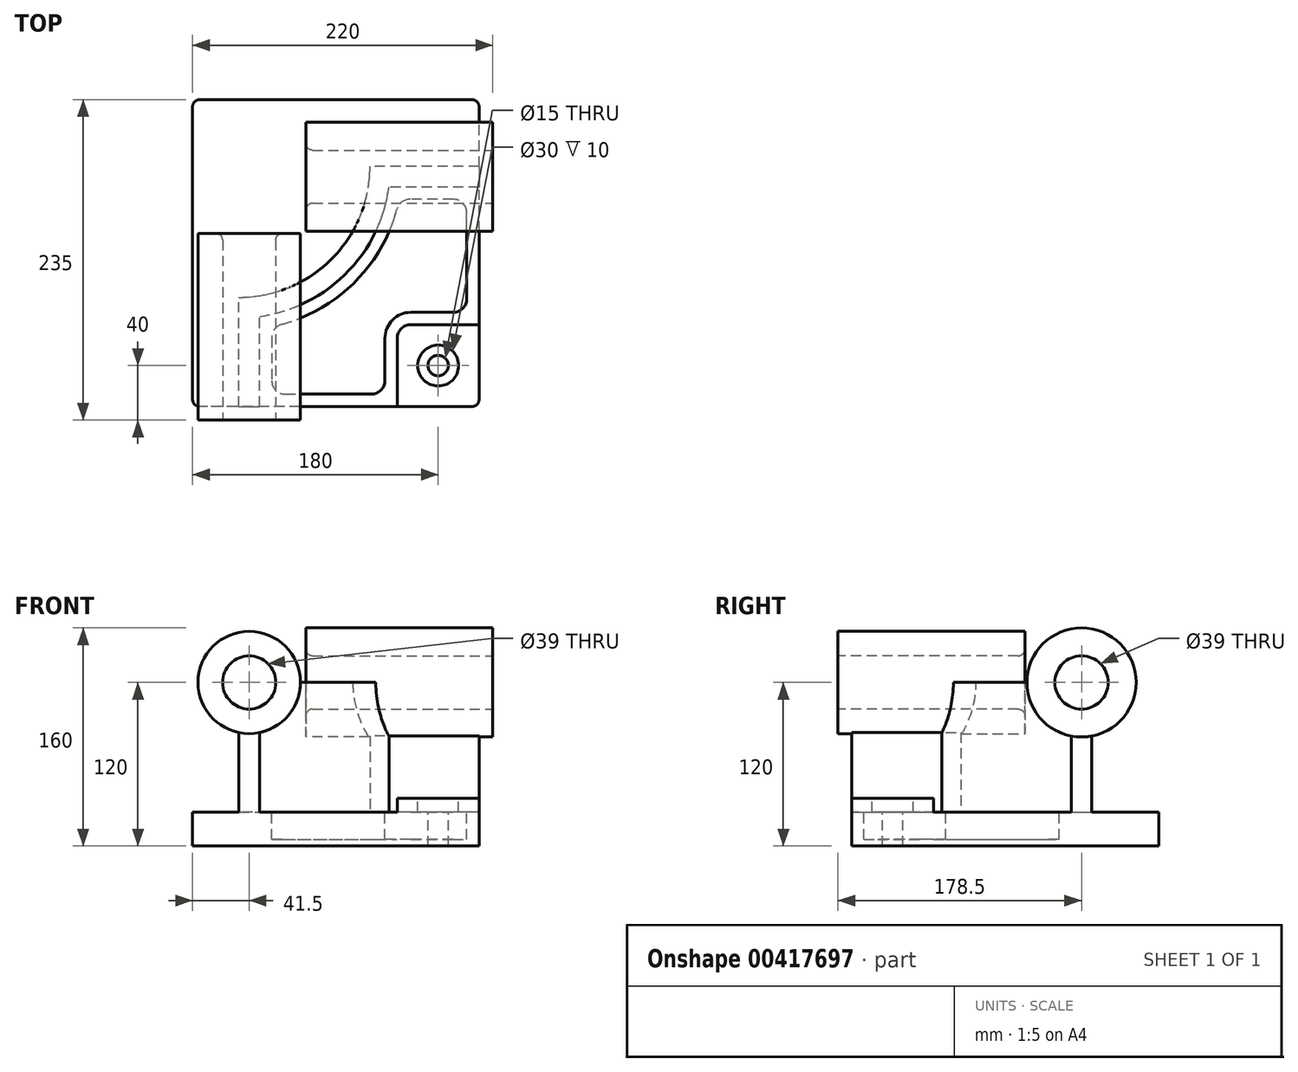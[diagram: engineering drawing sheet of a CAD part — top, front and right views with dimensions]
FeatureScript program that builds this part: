
annotation { "Feature Type Name" : "Feature", "Feature Type Description" : "" }
export const myFeature = defineFeature(function(context is Context, id is Id, definition is map)
    precondition{}
    {
        {
            var Q0;
            Q0=qCreatedBy(makeId("Top.planeOp"),FACE);
            var sketch = newSketch(context, id + "F0", { "sketchPlane" : qUnion([Q0])});
            skLineSegment(sketch, "E0.bottom", {"start": v(105, -112.5) * mm, "end": v(-105, -112.5) * mm});
            skLineSegment(sketch, "E0.top", {"start": v(105, 112.5) * mm, "end": v(-105, 112.5) * mm});
            skLineSegment(sketch, "E0.left", {"start": v(105, -112.5) * mm, "end": v(105, 112.5) * mm});
            skLineSegment(sketch, "E0.right", {"start": v(-105, -112.5) * mm, "end": v(-105, 112.5) * mm});
            skPoint(sketch, "E0.middle", {"position": v(0, 0) * mm});
            skSolve(sketch);
        }
        {
            var Q0;
            Q0=makeQuery(id+"F0.imprint","IMPRINT",FACE,{"disambiguationData":[TD([[makeQuery(id+"F0.imprint","IMPRINT",EDGE,{"derivedFrom":sQuery(id+"F0.wireOp",EDGE,"E0.bottom")}),-1.0]])]});
            extrude(context, id + "F1", {"entities" : qUnion([Q0]), "depth" : 25 * mm});
        }
        {
            var Q0;
            Q0=makeQuery(id+"F1.opExtrude","CAP_FACE",FACE,{"disambiguationData":[OSD([sQuery(id+"F0.wireOp",EDGE,"E0.bottom"),sQuery(id+"F0.wireOp",EDGE,"E0.top"),sQuery(id+"F0.wireOp",EDGE,"E0.left"),sQuery(id+"F0.wireOp",EDGE,"E0.right")])],"isStart":false});
            var sketch = newSketch(context, id + "F2", { "sketchPlane" : qUnion([Q0])});
            skLineSegment(sketch, "E1", {"start": v(-71, -112.5) * mm, "end": v(-71, -32.5) * mm});
            skLineSegment(sketch, "E2", {"start": v(105, 63.5) * mm, "end": v(25, 63.5) * mm});
            skArc(sketch, "E3", {"start": v(-71, -32.5) * mm, "mid": v(-3.12, -4.38) * mm, "end": v(25, 63.5) * mm});
            skLineSegment(sketch, "E4", {"start": v(-71, 63.5) * mm, "end": v(25, 63.5) * mm, "construction": true});
            skLineSegment(sketch, "E5", {"start": v(-71, 63.5) * mm, "end": v(-71, -32.5) * mm, "construction": true});
            skLineSegment(sketch, "E6.0", {"start": v(105, 48.5) * mm, "end": v(38.98, 48.5) * mm});
            skArc(sketch, "E6.1", {"start": v(-56, -46.48) * mm, "mid": v(7.49, -14.99) * mm, "end": v(38.98, 48.5) * mm});
            skLineSegment(sketch, "E6.2", {"start": v(-56, -112.5) * mm, "end": v(-56, -46.48) * mm});
            skLineSegment(sketch, "E7.0", {"start": v(105, -112.5) * mm, "end": v(-105, -112.5) * mm});
            skLineSegment(sketch, "E8.0", {"start": v(105, -112.5) * mm, "end": v(105, 112.5) * mm});
            skSolve(sketch);
        }
        {
            var Q0;
            {var subQ2=sQuery(id+"F2.wireOp",EDGE,"E1");Q0=makeQuery(id+"F2.imprint","IMPRINT",FACE,{"disambiguationData":[TD([[makeQuery(id+"F2.imprint","IMPRINT",EDGE,{"derivedFrom":subQ2}),-1.0]])]});}
            extrude(context, id + "F3", {"entities" : qUnion([Q0]), "operationType" : NewBodyOperationType.ADD, "depth" : 95 * mm});
        }
        {
            var Q0;
            Q0=makeQuery(id+"F3.boolean.opBoolean","MERGE",FACE,{"derivedFrom":[makeQuery(id+"F1.opExtrude","SWEPT_FACE",FACE,{"disambiguationData":[OSD([sQuery(id+"F0.wireOp",EDGE,"E0.bottom")])]}),makeQuery(id+"F3.opExtrude","SWEPT_FACE",FACE,{"disambiguationData":[OSD([sQuery(id+"F2.wireOp",EDGE,"E7.0")])]})]});
            var sketch = newSketch(context, id + "F4", { "sketchPlane" : qUnion([Q0])});
            skCircle(sketch, "E9", {"center": v(-63.5, 120) * mm, "radius": 37.5 * mm});
            skSolve(sketch);
        }
        {
            var Q0;
            Q0 = qSketchRegion(id + "F4", true);
            extrude(context, id + "F5", {"entities" : qUnion([Q0]), "operationType" : NewBodyOperationType.ADD, "depth" : 10 * mm, "hasSecondDirection" : true, "secondDirectionOppositeDirection" : true, "secondDirectionDepth" : 127 * mm});
        }
        {
            var Q0;
            Q0=makeQuery(id+"F3.boolean.opBoolean","MERGE",FACE,{"derivedFrom":[makeQuery(id+"F1.opExtrude","SWEPT_FACE",FACE,{"disambiguationData":[OSD([sQuery(id+"F0.wireOp",EDGE,"E0.left")])]}),makeQuery(id+"F3.opExtrude","SWEPT_FACE",FACE,{"disambiguationData":[OSD([sQuery(id+"F2.wireOp",EDGE,"E8.0")])]})]});
            var sketch = newSketch(context, id + "F6", { "sketchPlane" : qUnion([Q0])});
            skCircle(sketch, "E10", {"center": v(56, 120) * mm, "radius": 40 * mm});
            skSolve(sketch);
        }
        {
            var Q0;
            {var subQ1=sQuery(id+"F2.wireOp",EDGE,"E8.0");var subQ6=makeQuery(id+"F3.opExtrude","CAP_EDGE",EDGE,{"disambiguationData":[OSD([subQ1])],"isStart":false});Q0=makeQuery(id+"F6.imprint","IMPRINT",FACE,{"disambiguationData":[TD([[makeQuery(id+"F6.imprint","IMPRINT",EDGE,{"derivedFrom":subQ6}),-1.0]])]});}
            var Q1;
            {var subQ1=sQuery(id+"F2.wireOp",EDGE,"E8.0");var subQ6=makeQuery(id+"F3.opExtrude","CAP_EDGE",EDGE,{"disambiguationData":[OSD([subQ1])],"isStart":false});Q1=makeQuery(id+"F6.imprint","IMPRINT",FACE,{"disambiguationData":[TD([[makeQuery(id+"F6.imprint","IMPRINT",EDGE,{"derivedFrom":subQ6}),1.0]])]});}
            extrude(context, id + "F7", {"entities" : qUnion([Q0, Q1]), "operationType" : NewBodyOperationType.ADD, "depth" : 10 * mm, "hasSecondDirection" : true, "secondDirectionOppositeDirection" : true, "secondDirectionDepth" : 127 * mm});
        }
        {
            var Q0;
            {var subQ0=sQuery(id+"F0.wireOp",EDGE,"E0.left");var subQ1=sQuery(id+"F0.wireOp",EDGE,"E0.bottom");Q0=makeQuery(id+"F3.boolean.opBoolean","SPLIT",FACE,{"disambiguationData":[TD([makeQuery(id+"F3.opExtrude","SWEPT_FACE",FACE,{"disambiguationData":[OSD([sQuery(id+"F2.wireOp",EDGE,"E6.0")])]})])],"derivedFrom":makeQuery(id+"F1.opExtrude","CAP_FACE",FACE,{"disambiguationData":[OSD([subQ1,sQuery(id+"F0.wireOp",EDGE,"E0.top"),subQ0,sQuery(id+"F0.wireOp",EDGE,"E0.right")])],"isStart":false})});}
            var sketch = newSketch(context, id + "F8", { "sketchPlane" : qUnion([Q0])});
            skLineSegment(sketch, "E11.bottom", {"start": v(105, -112.5) * mm, "end": v(45, -112.5) * mm});
            skLineSegment(sketch, "E11.top", {"start": v(105, -52.5) * mm, "end": v(45, -52.5) * mm});
            skLineSegment(sketch, "E11.left", {"start": v(105, -112.5) * mm, "end": v(105, -52.5) * mm});
            skLineSegment(sketch, "E11.right", {"start": v(45, -112.5) * mm, "end": v(45, -52.5) * mm});
            skSolve(sketch);
        }
        {
            var Q0;
            Q0=makeQuery(id+"F8.imprint","IMPRINT",FACE,{"disambiguationData":[TD([[makeQuery(id+"F8.imprint","IMPRINT",EDGE,{"derivedFrom":sQuery(id+"F8.wireOp",EDGE,"E11.bottom")}),-1.0]])]});
            extrude(context, id + "F9", {"entities" : qUnion([Q0]), "operationType" : NewBodyOperationType.ADD, "depth" : 10 * mm});
        }
        {
            var Q0;
            Q0=makeQuery(id+"F9.opExtrude","SWEPT_EDGE",EDGE,{"disambiguationData":[OSD([sQuery(id+"F8.wireOp",EDGE,"E11.top"),sQuery(id+"F8.wireOp",EDGE,"E11.right")])]});
            fillet(context, id + "F10", {"entities" : qUnion([Q0]), "radius" : 10 * mm, "tangentPropagation" : true, "allowEdgeOverflow" : false});
        }
        {
            var Q0;
            {var subQ0=sQuery(id+"F0.wireOp",EDGE,"E0.left");var subQ1=sQuery(id+"F0.wireOp",EDGE,"E0.bottom");Q0=makeQuery(id+"F3.boolean.opBoolean","SPLIT",FACE,{"disambiguationData":[TD([makeQuery(id+"F3.opExtrude","SWEPT_FACE",FACE,{"disambiguationData":[OSD([sQuery(id+"F2.wireOp",EDGE,"E6.0")])]})])],"derivedFrom":makeQuery(id+"F1.opExtrude","CAP_FACE",FACE,{"disambiguationData":[OSD([subQ1,sQuery(id+"F0.wireOp",EDGE,"E0.top"),subQ0,sQuery(id+"F0.wireOp",EDGE,"E0.right")])],"isStart":false})});}
            var sketch = newSketch(context, id + "F11", { "sketchPlane" : qUnion([Q0])});
            skLineSegment(sketch, "E12.0", {"start": v(-47, -54.08) * mm, "end": v(-47, -103.5) * mm});
            skArc(sketch, "E12.1", {"start": v(46.58, 39.5) * mm, "mid": v(13.85, -21.35) * mm, "end": v(-47, -54.08) * mm});
            skLineSegment(sketch, "E12.2", {"start": v(-47, -103.5) * mm, "end": v(36, -103.5) * mm});
            skLineSegment(sketch, "E12.3", {"start": v(96, 39.5) * mm, "end": v(46.58, 39.5) * mm});
            skLineSegment(sketch, "E12.4", {"start": v(36, -103.5) * mm, "end": v(36, -62.5) * mm});
            skArc(sketch, "E12.5", {"start": v(36, -62.5) * mm, "mid": v(41.56, -49.06) * mm, "end": v(55, -43.5) * mm});
            skLineSegment(sketch, "E12.6", {"start": v(55, -43.5) * mm, "end": v(96, -43.5) * mm});
            skLineSegment(sketch, "E12.7", {"start": v(96, -43.5) * mm, "end": v(96, 39.5) * mm});
            skSolve(sketch);
        }
        {
            var Q0;
            Q0=makeQuery(id+"F11.imprint","IMPRINT",FACE,{"disambiguationData":[TD([[makeQuery(id+"F11.imprint","IMPRINT",EDGE,{"derivedFrom":sQuery(id+"F11.wireOp",EDGE,"E12.0")}),1.0]])]});
            extrude(context, id + "F12", {"entities" : qUnion([Q0]), "operationType" : NewBodyOperationType.REMOVE, "oppositeDirection" : true, "depth" : 20 * mm});
        }
        {
            var Q0;
            Q0=makeQuery(id+"F9.opExtrude","CAP_FACE",FACE,{"disambiguationData":[OSD([sQuery(id+"F8.wireOp",EDGE,"E11.bottom"),sQuery(id+"F8.wireOp",EDGE,"E11.top"),sQuery(id+"F8.wireOp",EDGE,"E11.left"),sQuery(id+"F8.wireOp",EDGE,"E11.right")])],"isStart":false});
            var sketch = newSketch(context, id + "F13", { "sketchPlane" : qUnion([Q0])});
            skCircle(sketch, "E13", {"center": v(75, -82.5) * mm, "radius": 15 * mm});
            skSolve(sketch);
        }
        {
            var Q0;
            Q0=sQuery(id+"F13.wireOp",VERTEX,"E13.center");
            var Q1;
            Q1=makeQuery(id+"F1.opExtrude","SWEPT_BODY",BODY,{"disambiguationData":[OSD([sQuery(id+"F0.wireOp",EDGE,"E0.bottom"),sQuery(id+"F0.wireOp",EDGE,"E0.top"),sQuery(id+"F0.wireOp",EDGE,"E0.left"),sQuery(id+"F0.wireOp",EDGE,"E0.right")])]});
            hole(context, id + "F14", {"style" : HoleStyle.C_BORE, "endStyle" : HoleEndStyle.THROUGH, "holeDiameter" : 15 * mm, "cBoreDiameter" : 30 * mm, "cBoreDepth" : 10 * mm, "isTappedThrough" : true, "tappedDepth" : 12.7 * mm, "tapClearance" : 3, "locations" : qUnion([Q0]), "scope" : qUnion([Q1])});
        }
        {
            var Q0;
            Q0=makeQuery(id+"F12.boolean.opBoolean","COPY",EDGE,{"derivedFrom":makeQuery(id+"F12.opExtrude","SWEPT_EDGE",EDGE,{"disambiguationData":[OSD([sQuery(id+"F11.wireOp",EDGE,"E12.0"),sQuery(id+"F11.wireOp",EDGE,"E12.2")])]})});
            var Q1;
            Q1=makeQuery(id+"F12.boolean.opBoolean","COPY",EDGE,{"derivedFrom":makeQuery(id+"F12.opExtrude","SWEPT_EDGE",EDGE,{"disambiguationData":[OSD([sQuery(id+"F11.wireOp",EDGE,"E12.3"),sQuery(id+"F11.wireOp",EDGE,"E12.7")])]})});
            var Q2;
            Q2=makeQuery(id+"F12.boolean.opBoolean","COPY",EDGE,{"derivedFrom":makeQuery(id+"F12.opExtrude","SWEPT_EDGE",EDGE,{"disambiguationData":[OSD([sQuery(id+"F11.wireOp",EDGE,"E12.0"),sQuery(id+"F11.wireOp",EDGE,"E12.1")])]})});
            var Q3;
            Q3=makeQuery(id+"F12.boolean.opBoolean","COPY",EDGE,{"derivedFrom":makeQuery(id+"F12.opExtrude","SWEPT_EDGE",EDGE,{"disambiguationData":[OSD([sQuery(id+"F11.wireOp",EDGE,"E12.1"),sQuery(id+"F11.wireOp",EDGE,"E12.3")])]})});
            var Q4;
            Q4=makeQuery(id+"F12.boolean.opBoolean","COPY",EDGE,{"derivedFrom":makeQuery(id+"F12.opExtrude","SWEPT_EDGE",EDGE,{"disambiguationData":[OSD([sQuery(id+"F11.wireOp",EDGE,"E12.6"),sQuery(id+"F11.wireOp",EDGE,"E12.7")])]})});
            var Q5;
            Q5=makeQuery(id+"F12.boolean.opBoolean","COPY",EDGE,{"derivedFrom":makeQuery(id+"F12.opExtrude","SWEPT_EDGE",EDGE,{"disambiguationData":[OSD([sQuery(id+"F11.wireOp",EDGE,"E12.2"),sQuery(id+"F11.wireOp",EDGE,"E12.4")])]})});
            fillet(context, id + "F15", {"entities" : qUnion([Q0, Q1, Q2, Q3, Q4, Q5]), "radius" : 10 * mm, "tangentPropagation" : true, "allowEdgeOverflow" : false});
        }
        {
            var Q0;
            Q0=makeQuery(id+"F5.opExtrude","CAP_FACE",FACE,{"disambiguationData":[OSD([sQuery(id+"F4.wireOp",EDGE,"E9")])],"isStart":false});
            var sketch = newSketch(context, id + "F16", { "sketchPlane" : qUnion([Q0])});
            skCircle(sketch, "E14", {"center": v(-63.5, 120) * mm, "radius": 19.5 * mm});
            skSolve(sketch);
        }
        {
            var Q0;
            Q0=makeQuery(id+"F16.imprint","IMPRINT",FACE,{"disambiguationData":[TD([[makeQuery(id+"F16.imprint","IMPRINT",EDGE,{"derivedFrom":sQuery(id+"F16.wireOp",EDGE,"E14")}),1.0]])]});
            extrude(context, id + "F17", {"entities" : qUnion([Q0]), "operationType" : NewBodyOperationType.REMOVE, "endBound" : BoundingType.THROUGH_ALL, "oppositeDirection" : true, "depth" : 77.72 * mm});
        }
        {
            var Q0;
            Q0=makeQuery(id+"F7.opExtrude","CAP_FACE",FACE,{"disambiguationData":[OSD([sQuery(id+"F6.wireOp",EDGE,"E10")])],"isStart":false});
            var sketch = newSketch(context, id + "F18", { "sketchPlane" : qUnion([Q0])});
            skCircle(sketch, "E15", {"center": v(56, 120) * mm, "radius": 19.5 * mm});
            skSolve(sketch);
        }
        {
            var Q0;
            Q0=makeQuery(id+"F18.imprint","IMPRINT",FACE,{"disambiguationData":[TD([[makeQuery(id+"F18.imprint","IMPRINT",EDGE,{"derivedFrom":sQuery(id+"F18.wireOp",EDGE,"E15")}),1.0]])]});
            var Q1;
            Q1=sQuery(id+"F18.wireOp",EDGE,"E15");
            extrude(context, id + "F19", {"entities" : qUnion([Q0]), "operationType" : NewBodyOperationType.REMOVE, "surfaceEntities" : qUnion([Q1]), "endBound" : BoundingType.THROUGH_ALL, "oppositeDirection" : true, "depth" : 84.33 * mm});
        }
        {
            var Q0;
            Q0=makeQuery(id+"F1.opExtrude","SWEPT_EDGE",EDGE,{"disambiguationData":[OSD([sQuery(id+"F0.wireOp",EDGE,"E0.bottom"),sQuery(id+"F0.wireOp",EDGE,"E0.right")])]});
            var Q1;
            Q1=makeQuery(id+"F9.boolean.opBoolean","MERGE",EDGE,{"derivedFrom":[makeQuery(id+"F1.opExtrude","SWEPT_EDGE",EDGE,{"disambiguationData":[OSD([sQuery(id+"F0.wireOp",EDGE,"E0.bottom"),sQuery(id+"F0.wireOp",EDGE,"E0.left")])]}),makeQuery(id+"F9.opExtrude","SWEPT_EDGE",EDGE,{"disambiguationData":[OSD([sQuery(id+"F8.wireOp",EDGE,"E11.bottom"),sQuery(id+"F8.wireOp",EDGE,"E11.left")])]})]});
            var Q2;
            Q2=makeQuery(id+"F1.opExtrude","SWEPT_EDGE",EDGE,{"disambiguationData":[OSD([sQuery(id+"F0.wireOp",EDGE,"E0.top"),sQuery(id+"F0.wireOp",EDGE,"E0.left")])]});
            var Q3;
            Q3=makeQuery(id+"F1.opExtrude","SWEPT_EDGE",EDGE,{"disambiguationData":[OSD([sQuery(id+"F0.wireOp",EDGE,"E0.top"),sQuery(id+"F0.wireOp",EDGE,"E0.right")])]});
            var Q4;
            Q4=makeQuery(id+"F17.boolean.opBoolean","INTERSECT",EDGE,{"derivedFrom":[makeQuery(id+"F5.opExtrude","CAP_FACE",FACE,{"disambiguationData":[OSD([sQuery(id+"F4.wireOp",EDGE,"E9")])],"isStart":true}),makeQuery(id+"F17.opExtrude","SWEPT_FACE",FACE,{"disambiguationData":[OSD([sQuery(id+"F16.wireOp",EDGE,"E14")])]})]});
            var Q5;
            Q5=makeQuery(id+"F19.boolean.opBoolean","INTERSECT",EDGE,{"derivedFrom":[makeQuery(id+"F7.opExtrude","CAP_FACE",FACE,{"disambiguationData":[OSD([sQuery(id+"F6.wireOp",EDGE,"E10")])],"isStart":true}),makeQuery(id+"F19.opExtrude","SWEPT_FACE",FACE,{"disambiguationData":[OSD([sQuery(id+"F18.wireOp",EDGE,"E15")])]})]});
            var Q6;
            Q6=makeQuery(id+"F19.boolean.opBoolean","COPY",EDGE,{"derivedFrom":makeQuery(id+"F19.opExtrude","CAP_EDGE",EDGE,{"disambiguationData":[OSD([sQuery(id+"F18.wireOp",EDGE,"E15")])],"isStart":true})});
            var Q7;
            Q7=makeQuery(id+"F17.boolean.opBoolean","COPY",EDGE,{"derivedFrom":makeQuery(id+"F17.opExtrude","CAP_EDGE",EDGE,{"disambiguationData":[OSD([sQuery(id+"F16.wireOp",EDGE,"E14")])],"isStart":true})});
            fillet(context, id + "F20", {"entities" : qUnion([Q0, Q1, Q2, Q3, Q4, Q5, Q6, Q7]), "radius" : 5 * mm, "tangentPropagation" : true, "allowEdgeOverflow" : false});
        }
    });
